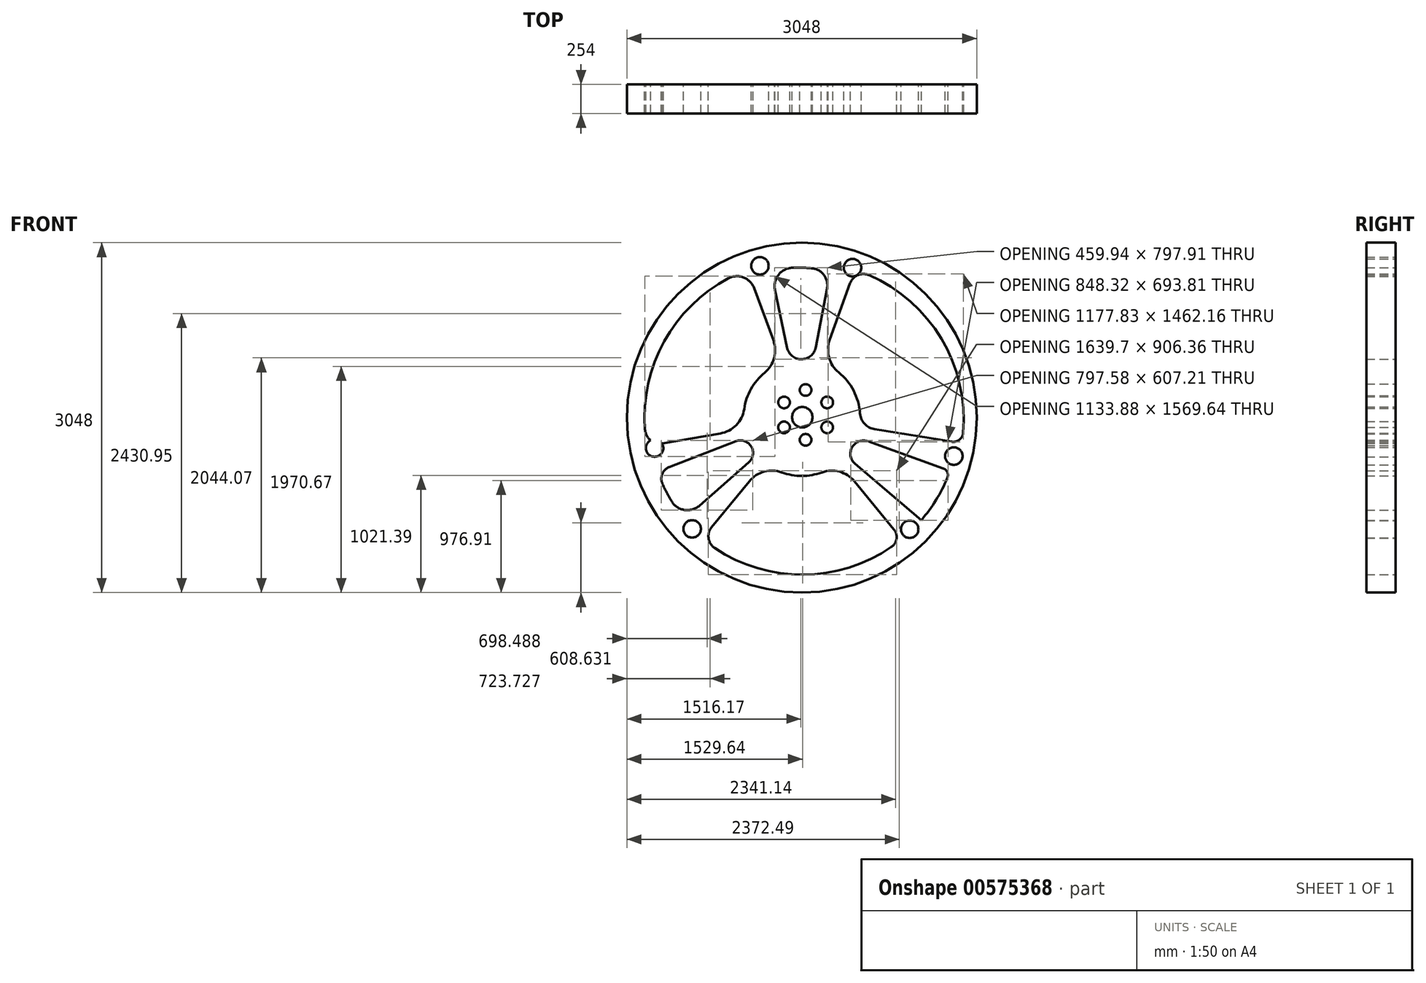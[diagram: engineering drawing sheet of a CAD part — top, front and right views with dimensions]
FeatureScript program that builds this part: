
annotation { "Feature Type Name" : "Feature", "Feature Type Description" : "" }
export const myFeature = defineFeature(function(context is Context, id is Id, definition is map)
    precondition{}
    {
        {
            var Q0;
            Q0=qCreatedBy(makeId("Front.planeOp"),FACE);
            var sketch = newSketch(context, id + "F0", { "sketchPlane" : qUnion([Q0])});
            skCircle(sketch, "E0", {"center": v(-32.43, -22.69) * mm, "radius": 1524 * mm});
            skPoint(sketch, "E1.center", {"position": v(-44.62, -19.06) * mm});
            skPoint(sketch, "E2.center", {"position": v(0, 0) * mm});
            skArc(sketch, "E3", {"start": v(-357.14, 367.99) * mm, "mid": v(-475.23, 226.28) * mm, "end": v(-534.94, 51.75) * mm});
            skLineSegment(sketch, "E4.trimOffspring", {"start": v(-398.24, 1299.14) * mm, "end": v(-438.9, 1446.1) * mm});
            skArc(sketch, "E5.trimOffspring", {"start": v(53.08, 1278.1) * mm, "mid": v(-30.77, 1282.8) * mm, "end": v(-114.74, 1282.35) * mm});
            skLineSegment(sketch, "E6.trimOffspring", {"start": v(350.16, 1373.53) * mm, "end": v(370.32, 1447.13) * mm});
            skLineSegment(sketch, "E7", {"start": v(-281.2, 651.28) * mm, "end": v(-448.79, 1105.26) * mm});
            skLineSegment(sketch, "E8", {"start": v(-160.88, 586.08) * mm, "end": v(-266.76, 1087.89) * mm});
            skLineSegment(sketch, "E9", {"start": v(210.6, 653.38) * mm, "end": v(388.42, 1148.09) * mm});
            skLineSegment(sketch, "E10", {"start": v(602.17, -124.67) * mm, "end": v(1274.5, -232.73) * mm});
            skLineSegment(sketch, "E11", {"start": v(543.23, -229.61) * mm, "end": v(1199.7, -465.59) * mm});
            skLineSegment(sketch, "E12", {"start": v(430.4, -424.14) * mm, "end": v(1007.96, -916.69) * mm});
            skLineSegment(sketch, "E13", {"start": v(424.43, -577.13) * mm, "end": v(769.04, -995.34) * mm});
            skLineSegment(sketch, "E14", {"start": v(-489.29, -577.13) * mm, "end": v(-818.35, -976.49) * mm});
            skLineSegment(sketch, "E15", {"start": v(-495.22, -413.54) * mm, "end": v(-924.92, -789.71) * mm});
            skLineSegment(sketch, "E16", {"start": v(-606.72, -229) * mm, "end": v(-1187.15, -452.74) * mm});
            skLineSegment(sketch, "E17", {"start": v(-742.92, -161.32) * mm, "end": v(-1244.43, -248.05) * mm});
            skPoint(sketch, "E18.orphan", {"position": v(-1474.28, -386.1) * mm});
            skArc(sketch, "E19.trimOffspring", {"start": v(-1247.33, -598.39) * mm, "mid": v(-1209.38, -676.73) * mm, "end": v(-1166.54, -752.52) * mm});
            skArc(sketch, "E20.trimOffspring", {"start": v(1372.11, -156.47) * mm, "mid": v(1183.05, 663.26) * mm, "end": v(551.02, 1218.44) * mm});
            skPoint(sketch, "E21.orphan", {"position": v(1071.51, -1083.72) * mm});
            skArc(sketch, "E22.trimOffspring", {"start": v(1007.96, -916.69) * mm, "mid": v(1136.51, -740.73) * mm, "end": v(1235.57, -546.63) * mm});
            skArc(sketch, "E23", {"start": v(-818.35, -976.49) * mm, "mid": v(-845.48, -1074.55) * mm, "end": v(-790.7, -1160.28) * mm});
            skPoint(sketch, "E24.orphan", {"position": v(-904.66, -1081.23) * mm});
            skArc(sketch, "E25", {"start": v(-1166.54, -752.52) * mm, "mid": v(-1054.4, -827.39) * mm, "end": v(-924.92, -789.71) * mm});
            skArc(sketch, "E26.trimOffspring", {"start": v(-790.7, -1160.28) * mm, "mid": v(-20.3, -1391.24) * mm, "end": v(747.14, -1150.6) * mm});
            skArc(sketch, "E27", {"start": v(-1187.15, -452.74) * mm, "mid": v(-1248.5, -512.65) * mm, "end": v(-1247.33, -598.39) * mm});
            skArc(sketch, "E28", {"start": v(-1398.9, -126.64) * mm, "mid": v(-1348.68, -221.72) * mm, "end": v(-1244.43, -248.05) * mm});
            skCircle(sketch, "E29", {"center": v(-32.43, -22.69) * mm, "radius": 381 * mm});
            skArc(sketch, "E30", {"start": v(-448.79, 1105.26) * mm, "mid": v(-540.92, 1198.55) * mm, "end": v(-671.8, 1190.77) * mm});
            skArc(sketch, "E31.trimOffspring", {"start": v(-671.8, 1190.77) * mm, "mid": v(-1232.14, 640.67) * mm, "end": v(-1398.9, -126.64) * mm});
            skArc(sketch, "E32", {"start": v(-114.74, 1282.35) * mm, "mid": v(-236.02, 1220.5) * mm, "end": v(-266.76, 1087.89) * mm});
            skLineSegment(sketch, "E33", {"start": v(88.09, 588.22) * mm, "end": v(187.03, 1100.7) * mm});
            skArc(sketch, "E34", {"start": v(187.03, 1100.7) * mm, "mid": v(159.53, 1219.2) * mm, "end": v(53.08, 1278.1) * mm});
            skArc(sketch, "E35", {"start": v(551.02, 1218.44) * mm, "mid": v(454.48, 1218.47) * mm, "end": v(388.42, 1148.09) * mm});
            skArc(sketch, "E36", {"start": v(1274.5, -232.73) * mm, "mid": v(1339.94, -215.88) * mm, "end": v(1372.11, -156.47) * mm});
            skLineSegment(sketch, "E37.trimOffspring", {"start": v(1336.25, -242.65) * mm, "end": v(1361.4, -246.7) * mm});
            skArc(sketch, "E38", {"start": v(1235.57, -546.63) * mm, "mid": v(1234.99, -498.43) * mm, "end": v(1199.7, -465.59) * mm});
            skArc(sketch, "E39", {"start": v(747.14, -1150.6) * mm, "mid": v(792.26, -1077.79) * mm, "end": v(769.04, -995.34) * mm});
            skLineSegment(sketch, "E40.trimOffspring", {"start": v(839.73, -1081.14) * mm, "end": v(839.8, -1081.23) * mm});
            skCircle(sketch, "E41", {"center": v(-398.24, 1299.14) * mm, "radius": 76.2 * mm});
            skCircle(sketch, "E42.1.0", {"center": v(-988.7, -992.32) * mm, "radius": 76.2 * mm});
            skCircle(sketch, "E42.2.0", {"center": v(1291, -357.94) * mm, "radius": 76.2 * mm});
            skPoint(sketch, "E42.center", {"position": v(-31.98, -17.04) * mm});
            skCircle(sketch, "E43", {"center": v(408.64, 1282.9) * mm, "radius": 76.2 * mm});
            skCircle(sketch, "E44.1.0", {"center": v(-1315.34, -287.55) * mm, "radius": 76.2 * mm});
            skCircle(sketch, "E44.2.0", {"center": v(906.7, -995.34) * mm, "radius": 76.2 * mm});
            skCircle(sketch, "E45", {"center": v(-28.93, -19.67) * mm, "radius": 88.9 * mm});
            skArc(sketch, "E46", {"start": v(-742.92, -161.32) * mm, "mid": v(-604.44, -88.45) * mm, "end": v(-534.94, 51.75) * mm});
            skArc(sketch, "E47", {"start": v(-357.14, 367.99) * mm, "mid": v(-274.15, 497.57) * mm, "end": v(-281.2, 651.28) * mm});
            skArc(sketch, "E48", {"start": v(-160.88, 586.08) * mm, "mid": v(-35.52, 485.3) * mm, "end": v(88.09, 588.22) * mm});
            skArc(sketch, "E49", {"start": v(210.6, 653.38) * mm, "mid": v(204.85, 499.61) * mm, "end": v(288.94, 370.74) * mm});
            skArc(sketch, "E50", {"start": v(474.2, 14.75) * mm, "mid": v(513.96, -77.2) * mm, "end": v(602.17, -124.67) * mm});
            skArc(sketch, "E51", {"start": v(543.23, -229.61) * mm, "mid": v(405.69, -279.83) * mm, "end": v(430.4, -424.14) * mm});
            skArc(sketch, "E52.trimOffspring", {"start": v(474.2, 14.75) * mm, "mid": v(418.2, 211.82) * mm, "end": v(288.94, 370.74) * mm});
            skArc(sketch, "E53", {"start": v(424.43, -577.13) * mm, "mid": v(295.2, -493.6) * mm, "end": v(141.46, -500) * mm});
            skArc(sketch, "E54", {"start": v(-206.32, -500) * mm, "mid": v(-360.06, -493.6) * mm, "end": v(-489.29, -577.13) * mm});
            skArc(sketch, "E55.trimOffspring", {"start": v(-206.32, -500) * mm, "mid": v(-32.43, -530.69) * mm, "end": v(141.46, -500) * mm});
            skArc(sketch, "E56", {"start": v(-495.22, -413.54) * mm, "mid": v(-473.63, -274.54) * mm, "end": v(-606.72, -229) * mm});
            skCircle(sketch, "E57", {"center": v(0, 217.7) * mm, "radius": 50.8 * mm});
            skCircle(sketch, "E58.1.0", {"center": v(188.01, 109.15) * mm, "radius": 50.8 * mm});
            skCircle(sketch, "E58.2.0", {"center": v(188.01, -107.94) * mm, "radius": 50.8 * mm});
            skCircle(sketch, "E58.3.0", {"center": v(0, -216.5) * mm, "radius": 50.8 * mm});
            skCircle(sketch, "E58.4.0", {"center": v(-188.01, -107.94) * mm, "radius": 50.8 * mm});
            skCircle(sketch, "E58.5.0", {"center": v(-188.01, 109.15) * mm, "radius": 50.8 * mm});
            skPoint(sketch, "E58.center", {"position": v(0, 0.6) * mm});
            skLineSegment(sketch, "E58.anchor1", {"start": v(0, 0.6) * mm, "end": v(0, 217.7) * mm, "construction": true});
            skLineSegment(sketch, "E58.anchor2", {"start": v(0, 0.6) * mm, "end": v(-188.01, 109.15) * mm, "construction": true});
            skSolve(sketch);
        }
        {
            var Q0;
            Q0 = qSketchRegion(id + "F0", true);
            var Q1;
            Q1=makeQuery(id+"F0.imprint","IMPRINT",FACE,{"disambiguationData":[TD([[makeQuery(id+"F0.imprint","IMPRINT",EDGE,{"derivedFrom":sQuery(id+"F0.wireOp",EDGE,"m696QnCD-Dlo9-7mFf-fxzx-CwewNaNtFx3B")}),-1.0]])]});
            var Q2;
            Q2=makeQuery(id+"F0.imprint","IMPRINT",FACE,{"disambiguationData":[TD([[makeQuery(id+"F0.imprint","IMPRINT",EDGE,{"derivedFrom":sQuery(id+"F0.wireOp",EDGE,"E29")}),-1.0]])]});
            var Q3;
            Q3=makeQuery(id+"F0.imprint","IMPRINT",FACE,{"disambiguationData":[TD([[makeQuery(id+"F0.imprint","IMPRINT",EDGE,{"derivedFrom":sQuery(id+"F0.wireOp",EDGE,"E29")}),1.0]])]});
            extrude(context, id + "F1", {"entities" : qUnion([Q0, Q1, Q2, Q3]), "depth" : 254 * mm, "offsetDistance" : 25.4 * mm});
        }
        {
            var Q0;
            Q0 = qSketchRegion(id + "F0", true);
            extrude(context, id + "F2", {"entities" : qUnion([Q0]), "operationType" : NewBodyOperationType.ADD, "depth" : 25.4 * mm, "offsetDistance" : 25.4 * mm});
        }
    });
